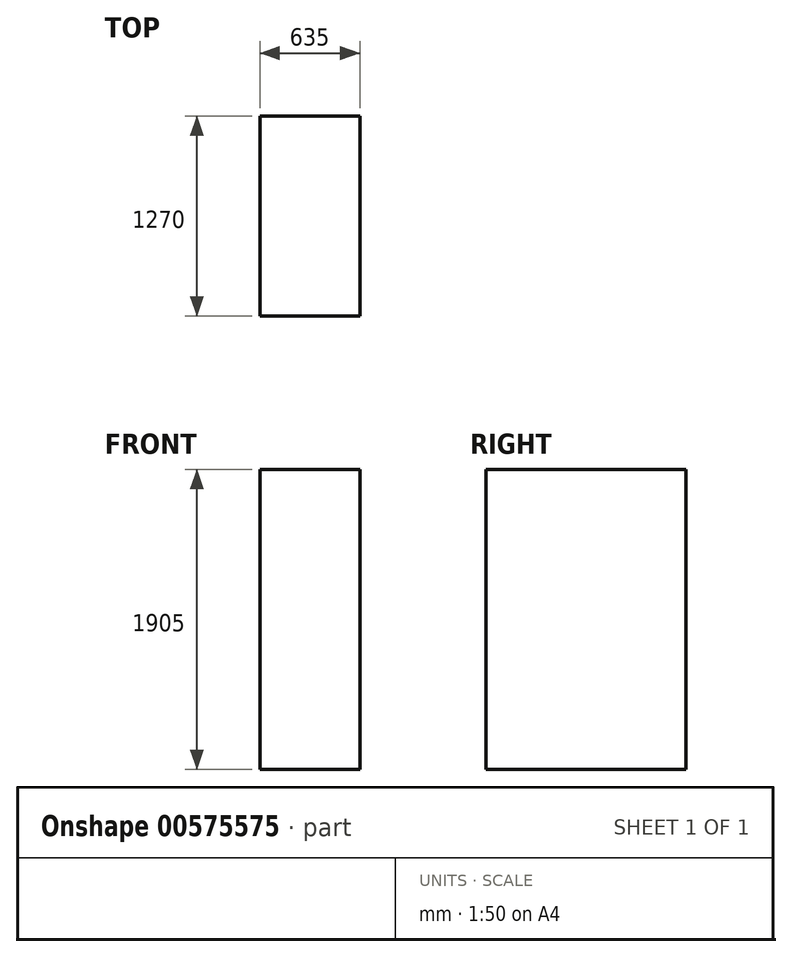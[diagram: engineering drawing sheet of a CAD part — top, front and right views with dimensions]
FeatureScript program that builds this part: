
annotation { "Feature Type Name" : "Feature", "Feature Type Description" : "" }
export const myFeature = defineFeature(function(context is Context, id is Id, definition is map)
    precondition{}
    {
        {
            var Q0;
            Q0=qCreatedBy(makeId("Top.planeOp"),FACE);
            var sketch = newSketch(context, id + "F0", { "sketchPlane" : qUnion([Q0])});
            skLineSegment(sketch, "E0.bottom", {"start": v(0, 0) * mm, "end": v(635, 0) * mm});
            skLineSegment(sketch, "E0.top", {"start": v(0, 1270) * mm, "end": v(635, 1270) * mm});
            skLineSegment(sketch, "E0.left", {"start": v(0, 0) * mm, "end": v(0, 1270) * mm});
            skLineSegment(sketch, "E0.right", {"start": v(635, 0) * mm, "end": v(635, 1270) * mm});
            skSolve(sketch);
        }
        {
            var Q0;
            Q0=makeQuery(id+"F0.imprint","IMPRINT",FACE,{"disambiguationData":[TD([[makeQuery(id+"F0.imprint","IMPRINT",EDGE,{"derivedFrom":sQuery(id+"F0.wireOp",EDGE,"E0.bottom")}),1.0]])]});
            extrude(context, id + "F1", {"entities" : qUnion([Q0]), "depth" : 1905 * mm, "offsetDistance" : 25.4 * mm});
        }
    });
